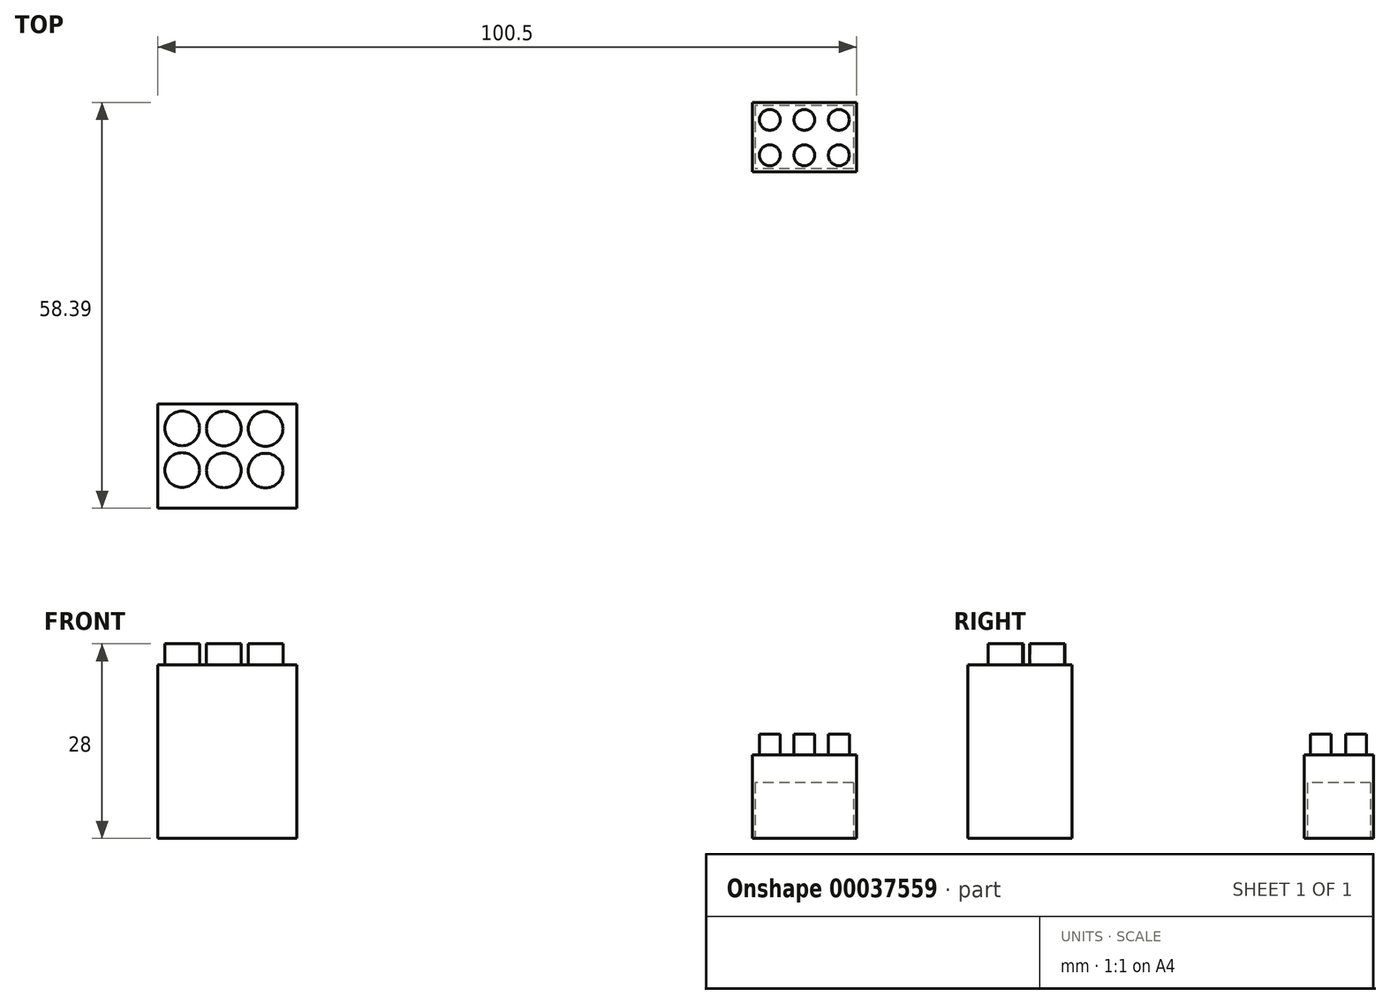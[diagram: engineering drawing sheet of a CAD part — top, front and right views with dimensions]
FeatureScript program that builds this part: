
annotation { "Feature Type Name" : "Feature", "Feature Type Description" : "" }
export const myFeature = defineFeature(function(context is Context, id is Id, definition is map)
    precondition{}
    {
        {
            var Q0;
            Q0=qCreatedBy(makeId("Top.planeOp"),FACE);
            var sketch = newSketch(context, id + "F0", { "sketchPlane" : qUnion([Q0])});
            skLineSegment(sketch, "E0.rect.bottom", {"start": v(7.5, 5) * mm, "end": v(-7.5, 5) * mm});
            skLineSegment(sketch, "E0.rect.top", {"start": v(7.5, -5) * mm, "end": v(-7.5, -5) * mm});
            skLineSegment(sketch, "E0.rect.left", {"start": v(7.5, 5) * mm, "end": v(7.5, -5) * mm});
            skLineSegment(sketch, "E0.rect.right", {"start": v(-7.5, 5) * mm, "end": v(-7.5, -5) * mm});
            skPoint(sketch, "E0.rect.middle", {"position": v(0, 0) * mm});
            skSolve(sketch);
        }
        {
            var Q0;
            Q0 = qSketchRegion(id + "F0", true);
            extrude(context, id + "F1", {"entities" : qUnion([Q0]), "depth" : 12 * mm});
        }
        {
            var Q0;
            Q0=makeQuery(id+"F1.opExtrude","CAP_FACE",FACE,{"disambiguationData":[OSD([sQuery(id+"F0.wireOp",EDGE,"E0.rect.bottom"),sQuery(id+"F0.wireOp",EDGE,"E0.rect.top"),sQuery(id+"F0.wireOp",EDGE,"E0.rect.left"),sQuery(id+"F0.wireOp",EDGE,"E0.rect.right")])],"isStart":false});
            var sketch = newSketch(context, id + "F2", { "sketchPlane" : qUnion([Q0])});
            skCircle(sketch, "E1", {"center": v(-4.97, -2.6) * mm, "radius": 1.5 * mm});
            skCircle(sketch, "E2", {"center": v(-4.97, 2.49) * mm, "radius": 1.5 * mm});
            skCircle(sketch, "E3", {"center": v(0, 2.49) * mm, "radius": 1.5 * mm});
            skCircle(sketch, "E4", {"center": v(0, -2.6) * mm, "radius": 1.5 * mm});
            skCircle(sketch, "E5", {"center": v(4.97, -2.6) * mm, "radius": 1.5 * mm});
            skCircle(sketch, "E6", {"center": v(4.97, 2.49) * mm, "radius": 1.5 * mm});
            skPoint(sketch, "E7.centerSnap0", {"position": v(0, 5) * mm});
            skLineSegment(sketch, "E8", {"start": v(-4.97, 2.49) * mm, "end": v(4.97, 2.49) * mm, "construction": true});
            skLineSegment(sketch, "E9", {"start": v(-4.97, 2.49) * mm, "end": v(-4.97, -2.6) * mm, "construction": true});
            skLineSegment(sketch, "E10", {"start": v(4.97, 2.49) * mm, "end": v(4.97, -2.6) * mm, "construction": true});
            skLineSegment(sketch, "E11", {"start": v(-4.97, -2.6) * mm, "end": v(4.97, -2.6) * mm, "construction": true});
            skLineSegment(sketch, "E12", {"start": v(0, 5) * mm, "end": v(0, 2.49) * mm, "construction": true});
            skSolve(sketch);
        }
        {
            var Q0;
            Q0 = qSketchRegion(id + "F2", true);
            extrude(context, id + "F3", {"entities" : qUnion([Q0]), "operationType" : NewBodyOperationType.ADD, "depth" : 3 * mm});
        }
        {
            var Q0;
            Q0=qCreatedBy(makeId("Top.planeOp"),FACE);
            var sketch = newSketch(context, id + "F4", { "sketchPlane" : qUnion([Q0])});
            skLineSegment(sketch, "E13.bottom", {"start": v(-93, -38.4) * mm, "end": v(-73, -38.4) * mm});
            skLineSegment(sketch, "E13.top", {"start": v(-93, -53.4) * mm, "end": v(-73, -53.4) * mm});
            skLineSegment(sketch, "E13.left", {"start": v(-93, -38.4) * mm, "end": v(-93, -53.4) * mm});
            skLineSegment(sketch, "E13.right", {"start": v(-73, -38.4) * mm, "end": v(-73, -53.4) * mm});
            skSolve(sketch);
        }
        {
            var Q0;
            Q0=makeQuery(id+"F4.imprint","IMPRINT",FACE,{"disambiguationData":[TD([[makeQuery(id+"F4.imprint","IMPRINT",EDGE,{"derivedFrom":sQuery(id+"F4.wireOp",EDGE,"E13.bottom")}),-1.0]])]});
            extrude(context, id + "F5", {"entities" : qUnion([Q0]), "depth" : 25 * mm});
        }
        {
            var Q0;
            Q0=makeQuery(id+"F5.opExtrude","CAP_FACE",FACE,{"disambiguationData":[OSD([sQuery(id+"F4.wireOp",EDGE,"E13.bottom"),sQuery(id+"F4.wireOp",EDGE,"E13.top"),sQuery(id+"F4.wireOp",EDGE,"E13.left"),sQuery(id+"F4.wireOp",EDGE,"E13.right")])],"isStart":false});
            var sketch = newSketch(context, id + "F6", { "sketchPlane" : qUnion([Q0])});
            skCircle(sketch, "E14", {"center": v(-89.5, -47.9) * mm, "radius": 2.5 * mm});
            skCircle(sketch, "E15.0.1.0", {"center": v(-89.5, -41.9) * mm, "radius": 2.5 * mm});
            skCircle(sketch, "E15.1.0.0", {"center": v(-83.5, -47.93) * mm, "radius": 2.5 * mm});
            skCircle(sketch, "E15.1.1.0", {"center": v(-83.5, -41.93) * mm, "radius": 2.5 * mm});
            skCircle(sketch, "E15.2.0.0", {"center": v(-77.5, -47.97) * mm, "radius": 2.5 * mm});
            skCircle(sketch, "E15.2.1.0", {"center": v(-77.5, -41.97) * mm, "radius": 2.5 * mm});
            skLineSegment(sketch, "E15.direction1", {"start": v(-89.5, -47.9) * mm, "end": v(-83.5, -47.93) * mm, "construction": true});
            skLineSegment(sketch, "E15.direction2", {"start": v(-89.5, -47.9) * mm, "end": v(-89.5, -41.9) * mm, "construction": true});
            skSolve(sketch);
        }
        {
            var Q0;
            Q0 = qSketchRegion(id + "F6", true);
            extrude(context, id + "F7", {"entities" : qUnion([Q0]), "operationType" : NewBodyOperationType.ADD, "depth" : 3 * mm});
        }
        {
            var Q0;
            Q0=makeQuery(id+"F1.opExtrude","CAP_FACE",FACE,{"disambiguationData":[OSD([sQuery(id+"F0.wireOp",EDGE,"E0.rect.bottom"),sQuery(id+"F0.wireOp",EDGE,"E0.rect.top"),sQuery(id+"F0.wireOp",EDGE,"E0.rect.left"),sQuery(id+"F0.wireOp",EDGE,"E0.rect.right")])],"isStart":true});
            var sketch = newSketch(context, id + "F8", { "sketchPlane" : qUnion([Q0])});
            skLineSegment(sketch, "E16.bottom", {"start": v(7.07, -4.55) * mm, "end": v(-7.08, -4.55) * mm});
            skLineSegment(sketch, "E16.top", {"start": v(7.07, 4.55) * mm, "end": v(-7.08, 4.55) * mm});
            skLineSegment(sketch, "E16.left", {"start": v(7.07, -4.55) * mm, "end": v(7.07, 4.55) * mm});
            skLineSegment(sketch, "E16.right", {"start": v(-7.08, -4.55) * mm, "end": v(-7.08, 4.55) * mm});
            skSolve(sketch);
        }
        {
            var Q0;
            Q0 = qSketchRegion(id + "F8", true);
            extrude(context, id + "F9", {"entities" : qUnion([Q0]), "operationType" : NewBodyOperationType.REMOVE, "oppositeDirection" : true, "depth" : 8 * mm});
        }
        {
            var Q0;
            Q0=makeQuery(id+"F9.boolean.opBoolean","COPY",FACE,{"derivedFrom":makeQuery(id+"F9.opExtrude","CAP_FACE",FACE,{"disambiguationData":[OSD([sQuery(id+"F8.wireOp",EDGE,"E16.bottom"),sQuery(id+"F8.wireOp",EDGE,"E16.top"),sQuery(id+"F8.wireOp",EDGE,"E16.left"),sQuery(id+"F8.wireOp",EDGE,"E16.right")])],"isStart":false})});
            var sketch = newSketch(context, id + "F10", { "sketchPlane" : qUnion([Q0])});
            skCircle(sketch, "E17", {"center": v(-3.68, 0) * mm, "radius": 1.71 * mm});
            skCircle(sketch, "E18", {"center": v(-3.68, 0) * mm, "radius": 1.24 * mm});
            skCircle(sketch, "E19.1.0.0", {"center": v(4.03, 0) * mm, "radius": 1.71 * mm});
            skCircle(sketch, "E19.1.0.1", {"center": v(4.03, 0) * mm, "radius": 1.24 * mm});
            skLineSegment(sketch, "E19.direction1", {"start": v(-3.68, 0) * mm, "end": v(4.03, 0) * mm, "construction": true});
            skSolve(sketch);
        }
        {
            var Q0;
            Q0=sQuery(id+"F10.wireOp",EDGE,"E19.1.0.1");
            var Q1;
            Q1=sQuery(id+"F10.wireOp",EDGE,"E19.1.0.0");
            var Q2;
            Q2=sQuery(id+"F10.wireOp",EDGE,"E17");
            var Q3;
            Q3=sQuery(id+"F10.wireOp",EDGE,"E18");
            extrude(context, id + "F11", {"bodyType" : ToolBodyType.SURFACE, "surfaceEntities" : qUnion([Q0, Q1, Q2, Q3]), "depth" : 7 * mm});
        }
    });
